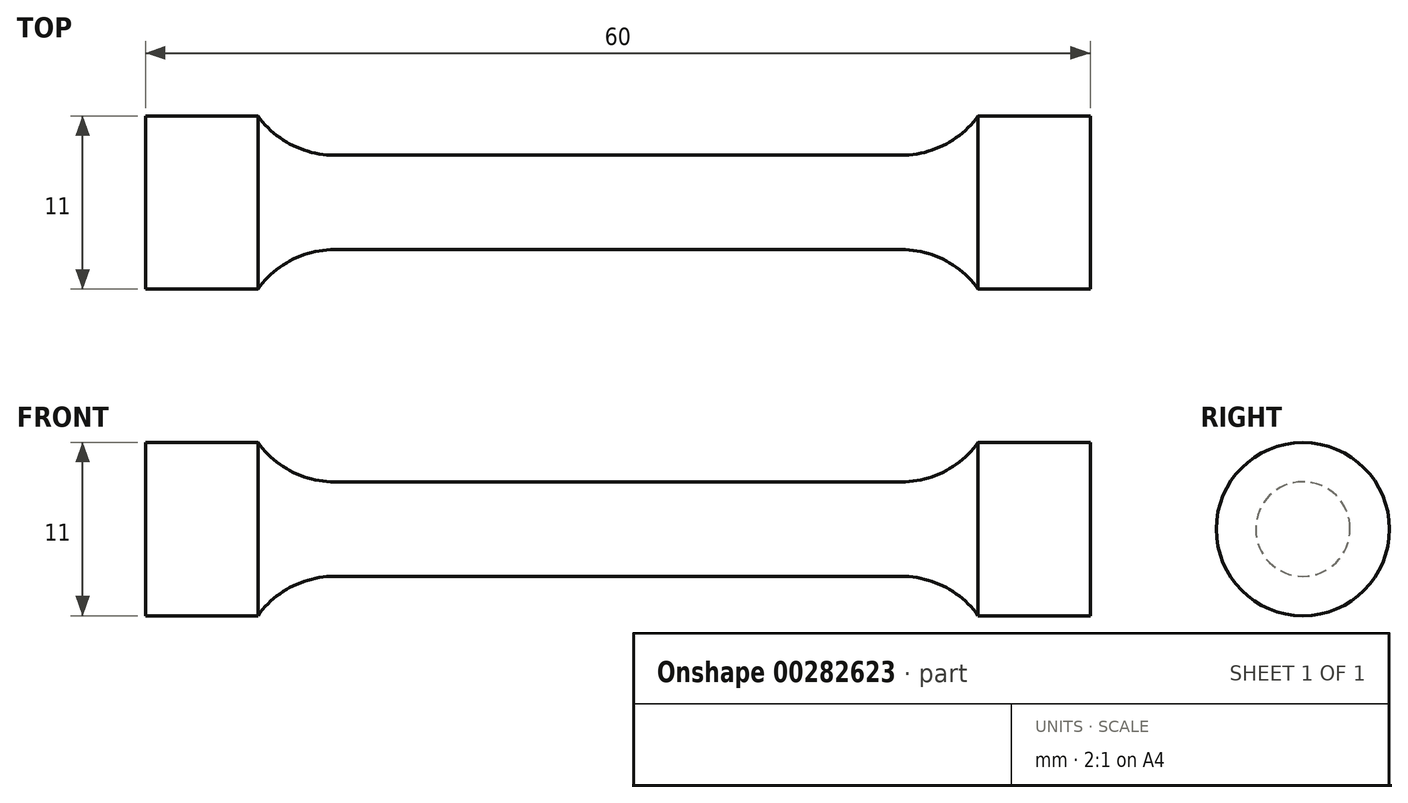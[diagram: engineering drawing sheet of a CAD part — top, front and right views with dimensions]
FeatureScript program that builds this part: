
annotation { "Feature Type Name" : "Feature", "Feature Type Description" : "" }
export const myFeature = defineFeature(function(context is Context, id is Id, definition is map)
    precondition{}
    {
        {
            var Q0;
            Q0=qCreatedBy(makeId("Front.planeOp"),FACE);
            var sketch = newSketch(context, id + "F0", { "sketchPlane" : qUnion([Q0])});
            skLineSegment(sketch, "E0", {"start": v(0, 3) * mm, "end": v(18, 3) * mm});
            skArc(sketch, "E1", {"start": v(18, 3) * mm, "mid": v(20.74, 3.66) * mm, "end": v(22.87, 5.5) * mm});
            skLineSegment(sketch, "E2", {"start": v(22.87, 5.5) * mm, "end": v(30, 5.5) * mm});
            skLineSegment(sketch, "E3", {"start": v(30, 5.5) * mm, "end": v(30, 0) * mm});
            skLineSegment(sketch, "E4", {"start": v(30, 0) * mm, "end": v(0, 0) * mm});
            skLineSegment(sketch, "E5.MirrorCS", {"start": v(0, 3) * mm, "end": v(-18, 3) * mm});
            skLineSegment(sketch, "E6.MirrorCS", {"start": v(-30, 0) * mm, "end": v(0, 0) * mm});
            skLineSegment(sketch, "E7.MirrorCS", {"start": v(-22.87, 5.5) * mm, "end": v(-30, 5.5) * mm});
            skLineSegment(sketch, "E8.MirrorCS", {"start": v(-30, 5.5) * mm, "end": v(-30, 0) * mm});
            skArc(sketch, "E9.MirrorCS", {"start": v(-18, 3) * mm, "mid": v(-20.74, 3.66) * mm, "end": v(-22.87, 5.5) * mm});
            skSolve(sketch);
        }
        {
            var Q0;
            Q0=makeQuery(id+"F0.imprint","IMPRINT",FACE,{"disambiguationData":[TD([[makeQuery(id+"F0.imprint","IMPRINT",EDGE,{"derivedFrom":sQuery(id+"F0.wireOp",EDGE,"E0")}),-1.0]])]});
            var Q1;
            Q1=sQuery(id+"F0.wireOp",EDGE,"E6.MirrorCS");
            revolve(context, id + "F1", {"entities" : qUnion([Q0]), "axis" : qUnion([Q1]), "revolveType" : RevolveType.FULL});
        }
    });
